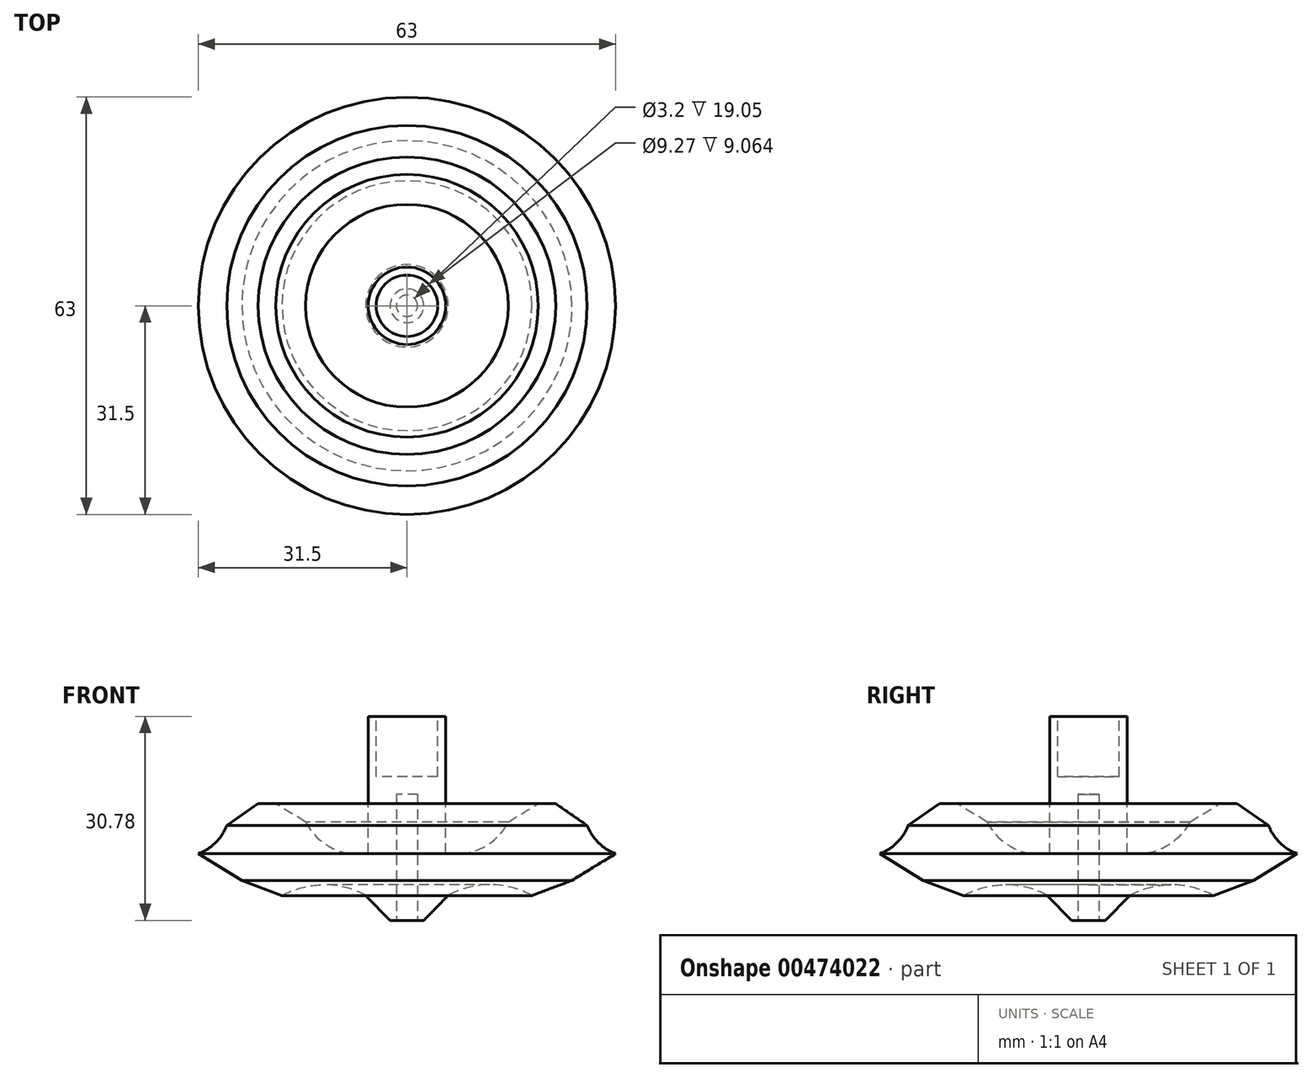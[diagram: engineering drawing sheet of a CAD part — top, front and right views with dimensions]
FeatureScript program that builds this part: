
annotation { "Feature Type Name" : "Feature", "Feature Type Description" : "" }
export const myFeature = defineFeature(function(context is Context, id is Id, definition is map)
    precondition{}
    {
        {
            var Q0;
            Q0=qCreatedBy(makeId("Front.planeOp"),FACE);
            var sketch = newSketch(context, id + "F0", { "sketchPlane" : qUnion([Q0])});
            skLineSegment(sketch, "E0", {"start": v(0, 30.83) * mm, "end": v(0, 0) * mm});
            skPoint(sketch, "E1.end.orphan", {"position": v(6.23, 17.6) * mm});
            skPoint(sketch, "E2", {"position": v(16.18, 17.6) * mm});
            skLineSegment(sketch, "E3", {"start": v(0, 0) * mm, "end": v(2.55, 0) * mm});
            skLineSegment(sketch, "E4", {"start": v(2.55, 0) * mm, "end": v(6.23, 3.77) * mm});
            skPoint(sketch, "E5.center.orphan", {"position": v(12.7, 17.6) * mm});
            skLineSegment(sketch, "E6", {"start": v(16.18, 17.6) * mm, "end": v(26.78, 17.6) * mm});
            skLineSegment(sketch, "E7", {"start": v(5.84, 30.77) * mm, "end": v(0, 30.83) * mm});
            skLineSegment(sketch, "E8", {"start": v(5.84, 30.77) * mm, "end": v(5.84, 17.6) * mm});
            skLineSegment(sketch, "E9", {"start": v(5.84, 17.6) * mm, "end": v(5.84, 10.16) * mm});
            skArc(sketch, "E10", {"start": v(5.84, 10.16) * mm, "mid": v(12.59, 11.7) * mm, "end": v(16.18, 17.6) * mm});
            skLineSegment(sketch, "E11", {"start": v(24.92, 6.03) * mm, "end": v(18.86, 3.74) * mm});
            skLineSegment(sketch, "E12", {"start": v(31.5, 10.07) * mm, "end": v(24.92, 6.03) * mm});
            skArc(sketch, "E13", {"start": v(18.86, 3.74) * mm, "mid": v(12.55, 5.38) * mm, "end": v(6.23, 3.77) * mm});
            skArc(sketch, "E14", {"start": v(26.78, 17.6) * mm, "mid": v(27.84, 13.03) * mm, "end": v(31.5, 10.07) * mm});
            skSolve(sketch);
        }
        {
            var Q0;
            Q0=qSketchRegion(id+"F0",true);
            var Q1;
            Q1=sQuery(id+"F0.wireOp",EDGE,"E0");
            revolve(context, id + "F1", {"entities" : qUnion([Q0]), "axis" : qUnion([Q1]), "revolveType" : RevolveType.FULL});
        }
        {
            var Q0;
            Q0=makeQuery(id+"F1.opRevolve","SWEPT_EDGE",EDGE,{"disambiguationData":[OSD([sQuery(id+"F0.wireOp",EDGE,"E6"),sQuery(id+"F0.wireOp",EDGE,"XC7HeOv8-VoYV-TnVc-6mjz-ZLLyT162wtiG")])]});
            chamfer(context, id + "F2", {"entities" : qUnion([Q0]), "width" : 5.08 * mm, "tangentPropagation" : true});
        }
        {
            var Q0;
            Q0=qCreatedBy(makeId("Top.planeOp"),FACE);
            var sketch = newSketch(context, id + "F3", { "sketchPlane" : qUnion([Q0])});
            skCircle(sketch, "E15", {"center": v(0, 0) * mm, "radius": 1.6 * mm});
            skSolve(sketch);
        }
        {
            var Q0;
            Q0=makeQuery(id+"F3.imprint","IMPRINT",FACE,{"disambiguationData":[TD([[makeQuery(id+"F3.imprint","IMPRINT",EDGE,{"derivedFrom":sQuery(id+"F3.wireOp",EDGE,"E15")}),1.0]])]});
            extrude(context, id + "F4", {"entities" : qUnion([Q0]), "operationType" : NewBodyOperationType.REMOVE, "depth" : 19.05 * mm});
        }
        {
            var Q0;
            Q0=qCreatedBy(makeId("Top.planeOp"),FACE);
            cPlane(context, id + "F5", {"entities" : qUnion([Q0]), "cplaneType" : CPlaneType.OFFSET, "offset" : 40.77 * mm, "width" : 152.4 * mm, "height" : 152.4 * mm});
        }
        {
            var Q0;
            Q0=qCreatedBy(id+"F5.planeOp",FACE);
            var sketch = newSketch(context, id + "F6", { "sketchPlane" : qUnion([Q0])});
            skCircle(sketch, "E16", {"center": v(0, 0) * mm, "radius": 4.64 * mm});
            skSolve(sketch);
        }
        {
            var Q0;
            Q0=makeQuery(id+"F6.imprint","IMPRINT",FACE,{"disambiguationData":[TD([[makeQuery(id+"F6.imprint","IMPRINT",EDGE,{"derivedFrom":sQuery(id+"F6.wireOp",EDGE,"E16")}),1.0]])]});
            extrude(context, id + "F7", {"entities" : qUnion([Q0]), "operationType" : NewBodyOperationType.REMOVE, "oppositeDirection" : true, "depth" : 19.05 * mm});
        }
    });
